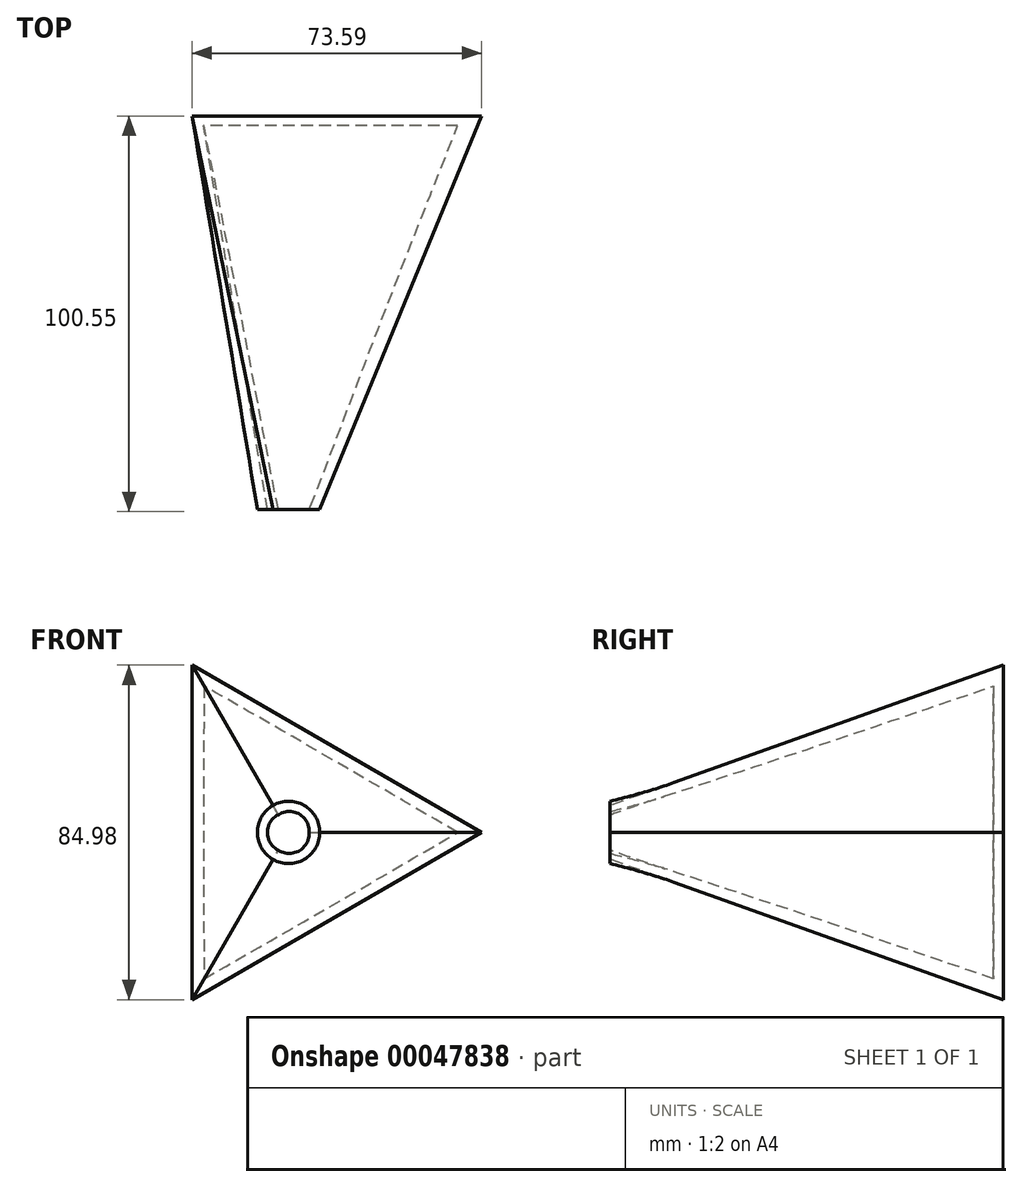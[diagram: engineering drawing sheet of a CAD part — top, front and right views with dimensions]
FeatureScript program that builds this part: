
annotation { "Feature Type Name" : "Feature", "Feature Type Description" : "" }
export const myFeature = defineFeature(function(context is Context, id is Id, definition is map)
    precondition{}
    {
        {
            var Q0;
            Q0=qCreatedBy(makeId("Front.planeOp"),FACE);
            var sketch = newSketch(context, id + "F0", { "sketchPlane" : qUnion([Q0])});
            skCircle(sketch, "E0.cCircle", {"center": v(0, 0) * mm, "radius": 24.53 * mm, "construction": true});
            skLineSegment(sketch, "E0.0", {"start": v(-24.53, -42.49) * mm, "end": v(-24.53, 42.49) * mm});
            skLineSegment(sketch, "E0.1", {"start": v(-24.53, 42.49) * mm, "end": v(49.06, 0) * mm});
            skLineSegment(sketch, "E0.2", {"start": v(49.06, 0) * mm, "end": v(-24.53, -42.49) * mm});
            skPoint(sketch, "E0.0.midPoint", {"position": v(-24.53, 0) * mm});
            skSolve(sketch);
        }
        {
            var Q0;
            Q0=qCreatedBy(makeId("Front.planeOp"),FACE);
            cPlane(context, id + "F1", {"entities" : qUnion([Q0]), "cplaneType" : CPlaneType.OFFSET, "offset" : 100 * mm, "width" : 152.4 * mm, "height" : 152.4 * mm});
        }
        {
            var Q0;
            Q0=qCreatedBy(id+"F1.planeOp",FACE);
            var sketch = newSketch(context, id + "F2", { "sketchPlane" : qUnion([Q0])});
            skCircle(sketch, "E1", {"center": v(0, 0) * mm, "radius": 7.91 * mm});
            skSolve(sketch);
        }
        {
            var Q0;
            Q0=makeQuery(id+"F0.imprint","IMPRINT",FACE,{"disambiguationData":[TD([[makeQuery(id+"F0.imprint","IMPRINT",EDGE,{"derivedFrom":sQuery(id+"F0.wireOp",EDGE,"E0.0")}),-1.0]])]});
            var Q1;
            Q1=makeQuery(id+"F2.imprint","IMPRINT",FACE,{"disambiguationData":[TD([[makeQuery(id+"F2.imprint","IMPRINT",EDGE,{"derivedFrom":sQuery(id+"F2.wireOp",EDGE,"E1")}),1.0]])]});
            loft(context, id + "F3", {"sheetProfilesArray" : [{ "sheetProfileEntities" : qUnion([Q0]) }, { "sheetProfileEntities" : qUnion([Q1]) }]});
        }
        {
            var Q0;
            Q0=makeQuery(id+"F3.opLoft","CAP_FACE",FACE,{"disambiguationData":[OSD([makeQuery(id+"F2.imprint","IMPRINT",FACE,{"disambiguationData":[TD([[makeQuery(id+"F2.imprint","IMPRINT",EDGE,{"derivedFrom":sQuery(id+"F2.wireOp",EDGE,"E1")}),1.0]])]})])],"isStart":true});
            shell(context, id + "F4", {"entities" : qUnion([Q0]), "thickness" : 2.5 * mm});
        }
    });
